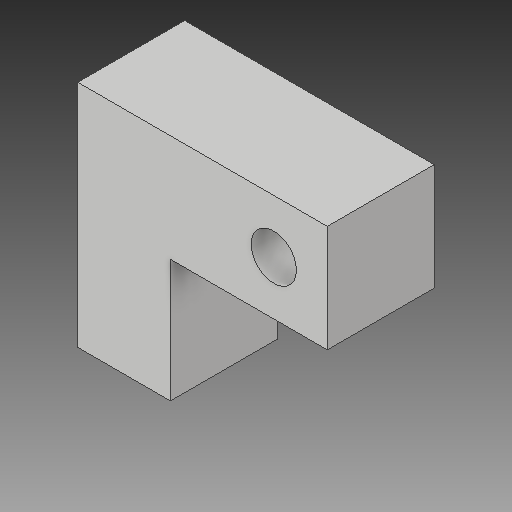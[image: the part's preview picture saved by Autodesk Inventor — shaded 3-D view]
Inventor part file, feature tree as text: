
AUTODESK INVENTOR PART (.ipt)
format: ipt  version: 2019 (Build 230136000, 136)  size: 123,904 bytes
history: native  units: mm
features: sketch x5, extrude x4, hole x1
ambient origin geometry x8: Origin, YZ Plane, XZ Plane, XY Plane, X Axis, Y Axis, Z Axis, Center Point
bodies: Solid1 (feature_tree)
feature tree (10):
  extrude  "Extrusion1"  Depth=322.0mm
  hole  "Hole1"  [1 undecoded]
  extrude  "Extrusion2"  Depth=150.0mm
  extrude  "Extrusion3"  Depth=172.0mm TaperAngle=0.0deg
  extrude  "Extrusion4"  Depth=130.0mm
  sketch  "Sketch1"  dims[d0=150.0mm d1=322.0mm]
  sketch  "Sketch2"  dims[d2=150.0mm d3=0.0mm d4=75.0mm]
  sketch  "Sketch3"  dims[d5=75.0mm]
  sketch  "Sketch4"  dims[d6=63.5mm d7=14.0mm d8=4.0mm d9=2.0mm d10=90.0deg d11=15.0mm d12=20.594885mm d13=150.0mm]
  sketch  "Sketch5"  dims[d14=200.0mm d15=0.0mm d16=172.0mm d17=0.0mm d18=130.0mm d19=172.0mm d20=0.0mm]
note: 1 required parameter value undecoded (feature->parameter linkage not recoverable at this tier; creation-order binding heuristic only, values carry confidence <= 0.55)
